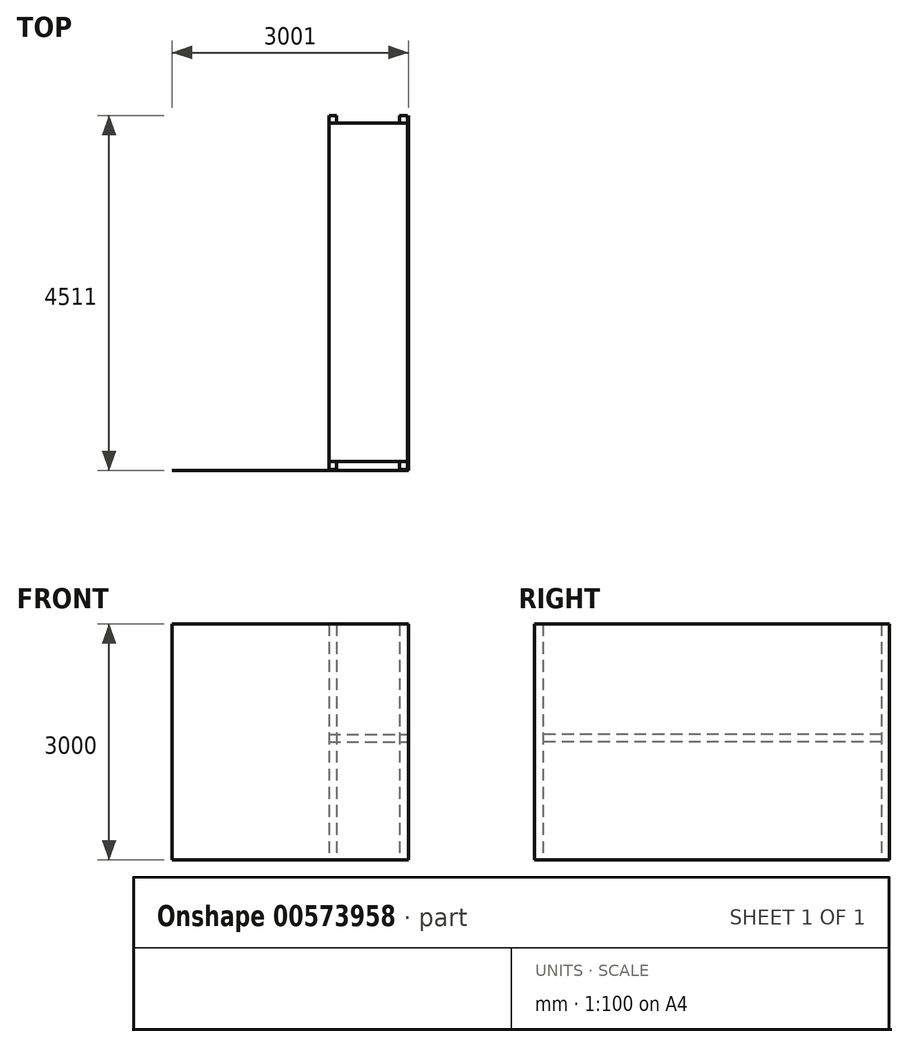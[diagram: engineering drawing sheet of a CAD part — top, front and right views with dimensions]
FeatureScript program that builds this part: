
annotation { "Feature Type Name" : "Feature", "Feature Type Description" : "" }
export const myFeature = defineFeature(function(context is Context, id is Id, definition is map)
    precondition{}
    {
        {
            var Q0;
            Q0=qCreatedBy(makeId("Top.planeOp"),FACE);
            cPlane(context, id + "F0", {"entities" : qUnion([Q0]), "cplaneType" : CPlaneType.OFFSET, "offset" : 1500 * mm, "width" : 150 * mm, "height" : 150 * mm});
        }
        {
            var Q0;
            Q0=qCreatedBy(makeId("Top.planeOp"),FACE);
            var sketch = newSketch(context, id + "F1", { "sketchPlane" : qUnion([Q0])});
            skPoint(sketch, "E0.middle", {"position": v(0, 0) * mm});
            skLineSegment(sketch, "E1.bottom", {"start": v(-500, 2250) * mm, "end": v(-400, 2250) * mm});
            skLineSegment(sketch, "E1.top", {"start": v(-500, 2150) * mm, "end": v(-400, 2150) * mm});
            skLineSegment(sketch, "E1.left", {"start": v(-500, 2250) * mm, "end": v(-500, 2150) * mm});
            skLineSegment(sketch, "E1.right", {"start": v(-400, 2250) * mm, "end": v(-400, 2150) * mm});
            skLineSegment(sketch, "E2.bottom", {"start": v(500, 2250) * mm, "end": v(400, 2250) * mm});
            skLineSegment(sketch, "E2.top", {"start": v(500, 2150) * mm, "end": v(400, 2150) * mm});
            skLineSegment(sketch, "E2.left", {"start": v(500, 2250) * mm, "end": v(500, 2150) * mm});
            skLineSegment(sketch, "E2.right", {"start": v(400, 2250) * mm, "end": v(400, 2150) * mm});
            skLineSegment(sketch, "E3.bottom", {"start": v(-500, -2250) * mm, "end": v(-400, -2250) * mm});
            skLineSegment(sketch, "E3.top", {"start": v(-500, -2150) * mm, "end": v(-400, -2150) * mm});
            skLineSegment(sketch, "E3.left", {"start": v(-500, -2250) * mm, "end": v(-500, -2150) * mm});
            skLineSegment(sketch, "E3.right", {"start": v(-400, -2250) * mm, "end": v(-400, -2150) * mm});
            skLineSegment(sketch, "E4.bottom", {"start": v(500, -2250) * mm, "end": v(400, -2250) * mm});
            skLineSegment(sketch, "E4.top", {"start": v(500, -2150) * mm, "end": v(400, -2150) * mm});
            skLineSegment(sketch, "E4.left", {"start": v(500, -2250) * mm, "end": v(500, -2150) * mm});
            skLineSegment(sketch, "E4.right", {"start": v(400, -2250) * mm, "end": v(400, -2150) * mm});
            skLineSegment(sketch, "E5.bottom", {"start": v(511, 2250) * mm, "end": v(510, 2250) * mm});
            skLineSegment(sketch, "E5.top", {"start": v(511, -2260) * mm, "end": v(510, -2260) * mm});
            skLineSegment(sketch, "E5.left", {"start": v(511, 2250) * mm, "end": v(511, -2260) * mm});
            skLineSegment(sketch, "E5.right", {"start": v(510, 2250) * mm, "end": v(510, -2260) * mm});
            skLineSegment(sketch, "E6.bottom", {"start": v(510, -2260) * mm, "end": v(-2490, -2260) * mm});
            skLineSegment(sketch, "E6.top", {"start": v(510, -2261) * mm, "end": v(-2490, -2261) * mm});
            skLineSegment(sketch, "E6.left", {"start": v(510, -2260) * mm, "end": v(510, -2261) * mm});
            skLineSegment(sketch, "E6.right", {"start": v(-2490, -2260) * mm, "end": v(-2490, -2261) * mm});
            skSolve(sketch);
        }
        {
            var Q0;
            Q0=qCreatedBy(id+"F0.planeOp",FACE);
            var sketch = newSketch(context, id + "F2", { "sketchPlane" : qUnion([Q0])});
            skLineSegment(sketch, "E7.bottom", {"start": v(-500, 2150) * mm, "end": v(500, 2150) * mm});
            skLineSegment(sketch, "E7.top", {"start": v(-500, -2150) * mm, "end": v(500, -2150) * mm});
            skLineSegment(sketch, "E7.left", {"start": v(-500, 2150) * mm, "end": v(-500, -2150) * mm});
            skLineSegment(sketch, "E7.right", {"start": v(500, 2150) * mm, "end": v(500, -2150) * mm});
            skPoint(sketch, "E7.middle", {"position": v(0, 0) * mm});
            skSolve(sketch);
        }
        {
            var Q0;
            Q0 = qSketchRegion(id + "F1", true);
            extrude(context, id + "F3", {"entities" : qUnion([Q0]), "depth" : 3000 * mm, "offsetDistance" : 25 * mm});
        }
        {
            var Q0;
            Q0 = qSketchRegion(id + "F2", true);
            extrude(context, id + "F4", {"entities" : qUnion([Q0]), "depth" : 100 * mm, "offsetDistance" : 25 * mm});
        }
    });
